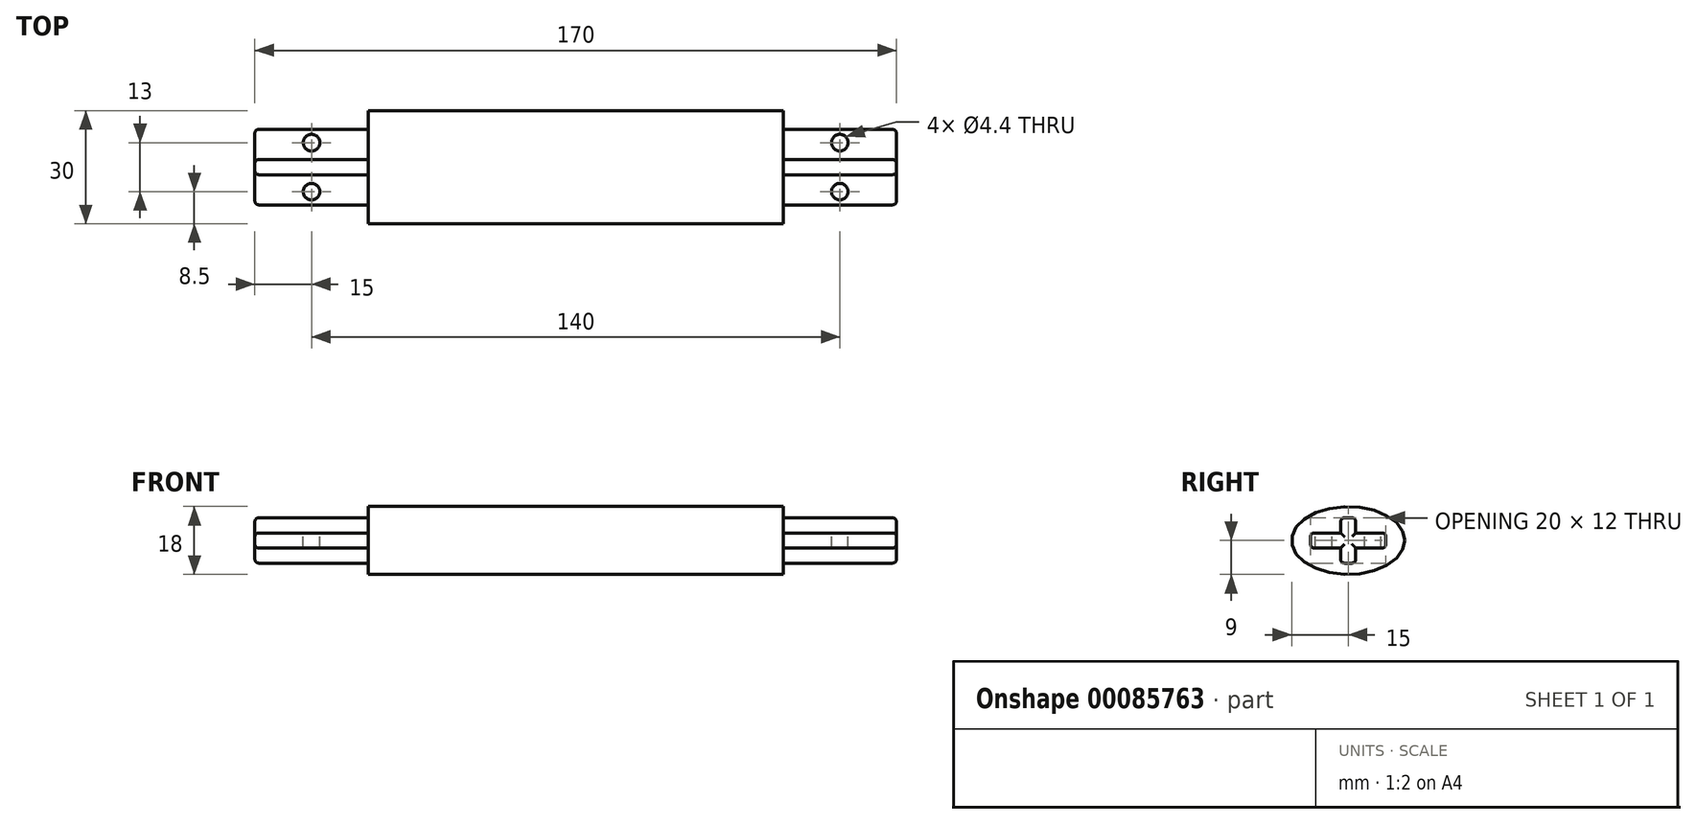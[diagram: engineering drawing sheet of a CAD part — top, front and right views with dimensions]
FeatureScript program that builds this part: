
annotation { "Feature Type Name" : "Feature", "Feature Type Description" : "" }
export const myFeature = defineFeature(function(context is Context, id is Id, definition is map)
    precondition{}
    {
        {
            var Q0;
            Q0=qCreatedBy(makeId("Right.planeOp"),FACE);
            var sketch = newSketch(context, id + "F0", { "sketchPlane" : qUnion([Q0])});
            skLineSegment(sketch, "E0", {"start": v(0, 6) * mm, "end": v(2, 6) * mm});
            skLineSegment(sketch, "E1", {"start": v(2, 6) * mm, "end": v(2, 2) * mm});
            skLineSegment(sketch, "E2", {"start": v(2, 2) * mm, "end": v(10, 2) * mm});
            skLineSegment(sketch, "E3", {"start": v(10, 2) * mm, "end": v(10, 0) * mm});
            skLineSegment(sketch, "E4.MirrorCS", {"start": v(-2, 2) * mm, "end": v(-10, 2) * mm});
            skLineSegment(sketch, "E5.MirrorCS", {"start": v(-2, 6) * mm, "end": v(-2, 2) * mm});
            skLineSegment(sketch, "E6.MirrorCS", {"start": v(0, 6) * mm, "end": v(-2, 6) * mm});
            skLineSegment(sketch, "E7.MirrorCS", {"start": v(-10, 2) * mm, "end": v(-10, 0) * mm});
            skLineSegment(sketch, "E8.MirrorCS", {"start": v(-2, -2) * mm, "end": v(-10, -2) * mm});
            skLineSegment(sketch, "E9.MirrorCS", {"start": v(-2, -6) * mm, "end": v(-2, -2) * mm});
            skLineSegment(sketch, "E10.MirrorCS", {"start": v(2, -6) * mm, "end": v(2, -2) * mm});
            skLineSegment(sketch, "E11.MirrorCS", {"start": v(0, -6) * mm, "end": v(-2, -6) * mm});
            skLineSegment(sketch, "E12.MirrorCS", {"start": v(10, -2) * mm, "end": v(10, 0) * mm});
            skLineSegment(sketch, "E13.MirrorCS", {"start": v(0, -6) * mm, "end": v(2, -6) * mm});
            skLineSegment(sketch, "E14.MirrorCS", {"start": v(-10, -2) * mm, "end": v(-10, 0) * mm});
            skLineSegment(sketch, "E15.MirrorCS", {"start": v(2, -2) * mm, "end": v(10, -2) * mm});
            skSolve(sketch);
        }
        {
            var Q0;
            Q0=makeQuery(id+"F0.imprint","IMPRINT",FACE,{"disambiguationData":[TD([[makeQuery(id+"F0.imprint","IMPRINT",EDGE,{"derivedFrom":sQuery(id+"F0.wireOp",EDGE,"E3")}),-1.0]])]});
            var Q1;
            Q1 = qConstructionFilter(qBodyType(qCreatedBy(id + "F0" ,EDGE), BodyType.WIRE), ConstructionObject.NO);
            extrude(context, id + "F1", {"entities" : qUnion([Q0]), "surfaceEntities" : qUnion([Q1]), "depth" : 170 * mm});
        }
        {
            var Q0;
            Q0=makeQuery(id+"F1.opExtrude","SWEPT_EDGE",EDGE,{"disambiguationData":[OSD([sQuery(id+"F0.wireOp",EDGE,"E1"),sQuery(id+"F0.wireOp",EDGE,"E0")])]});
            var Q1;
            Q1=makeQuery(id+"F1.opExtrude","SWEPT_EDGE",EDGE,{"disambiguationData":[OSD([sQuery(id+"F0.wireOp",EDGE,"E4.MirrorCS"),sQuery(id+"F0.wireOp",EDGE,"E7.MirrorCS")])]});
            var Q2;
            Q2=makeQuery(id+"F1.opExtrude","SWEPT_EDGE",EDGE,{"disambiguationData":[OSD([sQuery(id+"F0.wireOp",EDGE,"E6.MirrorCS"),sQuery(id+"F0.wireOp",EDGE,"E5.MirrorCS")])]});
            var Q3;
            Q3=makeQuery(id+"F1.opExtrude","SWEPT_EDGE",EDGE,{"disambiguationData":[OSD([sQuery(id+"F0.wireOp",EDGE,"E13.MirrorCS"),sQuery(id+"F0.wireOp",EDGE,"E10.MirrorCS")])]});
            var Q4;
            Q4=makeQuery(id+"F1.opExtrude","SWEPT_EDGE",EDGE,{"disambiguationData":[OSD([sQuery(id+"F0.wireOp",EDGE,"E12.MirrorCS"),sQuery(id+"F0.wireOp",EDGE,"E15.MirrorCS")])]});
            var Q5;
            Q5=makeQuery(id+"F1.opExtrude","SWEPT_EDGE",EDGE,{"disambiguationData":[OSD([sQuery(id+"F0.wireOp",EDGE,"E3"),sQuery(id+"F0.wireOp",EDGE,"E2")])]});
            var Q6;
            Q6=makeQuery(id+"F1.opExtrude","SWEPT_EDGE",EDGE,{"disambiguationData":[OSD([sQuery(id+"F0.wireOp",EDGE,"E14.MirrorCS"),sQuery(id+"F0.wireOp",EDGE,"E8.MirrorCS")])]});
            var Q7;
            Q7=makeQuery(id+"F1.opExtrude","SWEPT_EDGE",EDGE,{"disambiguationData":[OSD([sQuery(id+"F0.wireOp",EDGE,"E9.MirrorCS"),sQuery(id+"F0.wireOp",EDGE,"E11.MirrorCS")])]});
            var Q8;
            Q8=makeQuery(id+"F1.opExtrude","CAP_EDGE",EDGE,{"disambiguationData":[OSD([sQuery(id+"F0.wireOp",EDGE,"E5.MirrorCS")])],"isStart":false});
            var Q9;
            Q9=makeQuery(id+"F1.opExtrude","CAP_EDGE",EDGE,{"disambiguationData":[OSD([sQuery(id+"F0.wireOp",EDGE,"E1")])],"isStart":false});
            var Q10;
            Q10=makeQuery(id+"F1.opExtrude","CAP_EDGE",EDGE,{"disambiguationData":[OSD([sQuery(id+"F0.wireOp",EDGE,"E2")])],"isStart":false});
            var Q11;
            Q11=makeQuery(id+"F1.opExtrude","CAP_FACE",FACE,{"disambiguationData":[OSD([sQuery(id+"F0.wireOp",EDGE,"E3"),sQuery(id+"F0.wireOp",EDGE,"E4.MirrorCS"),sQuery(id+"F0.wireOp",EDGE,"E7.MirrorCS"),sQuery(id+"F0.wireOp",EDGE,"E2"),sQuery(id+"F0.wireOp",EDGE,"E6.MirrorCS"),sQuery(id+"F0.wireOp",EDGE,"E1"),sQuery(id+"F0.wireOp",EDGE,"E5.MirrorCS"),sQuery(id+"F0.wireOp",EDGE,"E0"),sQuery(id+"F0.wireOp",EDGE,"E13.MirrorCS"),sQuery(id+"F0.wireOp",EDGE,"E9.MirrorCS"),sQuery(id+"F0.wireOp",EDGE,"E12.MirrorCS"),sQuery(id+"F0.wireOp",EDGE,"E14.MirrorCS"),sQuery(id+"F0.wireOp",EDGE,"E10.MirrorCS"),sQuery(id+"F0.wireOp",EDGE,"E15.MirrorCS"),sQuery(id+"F0.wireOp",EDGE,"E11.MirrorCS"),sQuery(id+"F0.wireOp",EDGE,"E8.MirrorCS")])],"isStart":false});
            var Q12;
            Q12=makeQuery(id+"F1.opExtrude","CAP_EDGE",EDGE,{"disambiguationData":[OSD([sQuery(id+"F0.wireOp",EDGE,"E4.MirrorCS")])],"isStart":false});
            var Q13;
            Q13=makeQuery(id+"F1.opExtrude","CAP_EDGE",EDGE,{"disambiguationData":[OSD([sQuery(id+"F0.wireOp",EDGE,"E5.MirrorCS")])],"isStart":true});
            var Q14;
            Q14=makeQuery(id+"F1.opExtrude","CAP_EDGE",EDGE,{"disambiguationData":[OSD([sQuery(id+"F0.wireOp",EDGE,"E6.MirrorCS"),sQuery(id+"F0.wireOp",EDGE,"E0")])],"isStart":true});
            var Q15;
            Q15=makeQuery(id+"F1.opExtrude","CAP_EDGE",EDGE,{"disambiguationData":[OSD([sQuery(id+"F0.wireOp",EDGE,"E1")])],"isStart":true});
            var Q16;
            Q16=makeQuery(id+"F1.opExtrude","CAP_EDGE",EDGE,{"disambiguationData":[OSD([sQuery(id+"F0.wireOp",EDGE,"E4.MirrorCS")])],"isStart":true});
            var Q17;
            Q17=makeQuery(id+"F1.opExtrude","CAP_EDGE",EDGE,{"disambiguationData":[OSD([sQuery(id+"F0.wireOp",EDGE,"E8.MirrorCS")])],"isStart":true});
            var Q18;
            Q18=makeQuery(id+"F1.opExtrude","CAP_EDGE",EDGE,{"disambiguationData":[OSD([sQuery(id+"F0.wireOp",EDGE,"E7.MirrorCS"),sQuery(id+"F0.wireOp",EDGE,"E14.MirrorCS")])],"isStart":true});
            var Q19;
            Q19=makeQuery(id+"F1.opExtrude","CAP_EDGE",EDGE,{"disambiguationData":[OSD([sQuery(id+"F0.wireOp",EDGE,"E9.MirrorCS")])],"isStart":true});
            var Q20;
            Q20=makeQuery(id+"F1.opExtrude","CAP_EDGE",EDGE,{"disambiguationData":[OSD([sQuery(id+"F0.wireOp",EDGE,"E10.MirrorCS")])],"isStart":true});
            var Q21;
            Q21=makeQuery(id+"F1.opExtrude","CAP_EDGE",EDGE,{"disambiguationData":[OSD([sQuery(id+"F0.wireOp",EDGE,"E15.MirrorCS")])],"isStart":true});
            var Q22;
            Q22=makeQuery(id+"F1.opExtrude","CAP_EDGE",EDGE,{"disambiguationData":[OSD([sQuery(id+"F0.wireOp",EDGE,"E3"),sQuery(id+"F0.wireOp",EDGE,"E12.MirrorCS")])],"isStart":true});
            var Q23;
            Q23=makeQuery(id+"F1.opExtrude","CAP_EDGE",EDGE,{"disambiguationData":[OSD([sQuery(id+"F0.wireOp",EDGE,"E2")])],"isStart":true});
            var Q24;
            Q24=makeQuery(id+"F1.opExtrude","CAP_EDGE",EDGE,{"disambiguationData":[OSD([sQuery(id+"F0.wireOp",EDGE,"E13.MirrorCS"),sQuery(id+"F0.wireOp",EDGE,"E11.MirrorCS")])],"isStart":true});
            fillet(context, id + "F2", {"entities" : qUnion([Q0, Q1, Q2, Q3, Q4, Q5, Q6, Q7, Q8, Q9, Q10, Q11, Q12, Q13, Q14, Q15, Q16, Q17, Q18, Q19, Q20, Q21, Q22, Q23, Q24]), "radius" : 1 * mm, "tangentPropagation" : true, "allowEdgeOverflow" : false});
        }
        {
            var Q0;
            Q0=qCreatedBy(makeId("Top.planeOp"),FACE);
            cPlane(context, id + "F3", {"entities" : qUnion([Q0]), "cplaneType" : CPlaneType.OFFSET, "offset" : 15 * mm, "width" : 150 * mm, "height" : 150 * mm});
        }
        {
            var Q0;
            Q0=qCreatedBy(id+"F3.planeOp",FACE);
            var sketch = newSketch(context, id + "F4", { "sketchPlane" : qUnion([Q0])});
            skPoint(sketch, "E16", {"position": v(15, 6.5) * mm});
            skPoint(sketch, "E17", {"position": v(15, -6.5) * mm});
            skPoint(sketch, "E18", {"position": v(155, 6.5) * mm});
            skPoint(sketch, "E19", {"position": v(155, -6.5) * mm});
            skSolve(sketch);
        }
        {
            var Q0;
            Q0=qCreatedBy(makeId("Right.planeOp"),FACE);
            cPlane(context, id + "F5", {"entities" : qUnion([Q0]), "cplaneType" : CPlaneType.OFFSET, "offset" : 30 * mm, "width" : 150 * mm, "height" : 150 * mm});
        }
        {
            var Q0;
            Q0=qCreatedBy(id+"F5.planeOp",FACE);
            var sketch = newSketch(context, id + "F6", { "sketchPlane" : qUnion([Q0])});
            skEllipse(sketch, "E20", {"center": v(0, 0) * mm, "majorRadius": 15 * mm, "minorRadius": 9 * mm, "majorAxis": v(1, 0)});
            skLineSegment(sketch, "E21", {"start": v(0, 0) * mm, "end": v(15, 0) * mm});
            skLineSegment(sketch, "E22", {"start": v(0, 0) * mm, "end": v(0, 9) * mm});
            skSolve(sketch);
        }
        {
            var Q0;
            {var subQ0=sQuery(id+"F6.wireOp",EDGE,"E21");Q0=makeQuery(id+"F6.imprint","IMPRINT",FACE,{"disambiguationData":[TD([[makeQuery(id+"F6.imprint","IMPRINT",EDGE,{"derivedFrom":subQ0}),-1.0]])]});}
            var Q1;
            {var subQ0=sQuery(id+"F6.wireOp",EDGE,"E21");Q1=makeQuery(id+"F6.imprint","IMPRINT",FACE,{"disambiguationData":[TD([[makeQuery(id+"F6.imprint","IMPRINT",EDGE,{"derivedFrom":subQ0}),1.0]])]});}
            extrude(context, id + "F7", {"entities" : qUnion([Q0, Q1]), "operationType" : NewBodyOperationType.ADD, "depth" : 110 * mm});
        }
        {
            var Q0;
            Q0=sQuery(id+"F4.wireOp",VERTEX,"E16");
            var Q1;
            Q1=sQuery(id+"F4.wireOp",VERTEX,"E17");
            var Q2;
            Q2=sQuery(id+"F4.wireOp",VERTEX,"E19");
            var Q3;
            Q3=sQuery(id+"F4.wireOp",VERTEX,"E18");
            var Q4;
            Q4=makeQuery(id+"F1.opExtrude","SWEPT_BODY",BODY,{"disambiguationData":[OSD([sQuery(id+"F0.wireOp",EDGE,"E3"),sQuery(id+"F0.wireOp",EDGE,"E4.MirrorCS"),sQuery(id+"F0.wireOp",EDGE,"E7.MirrorCS"),sQuery(id+"F0.wireOp",EDGE,"E2"),sQuery(id+"F0.wireOp",EDGE,"E6.MirrorCS"),sQuery(id+"F0.wireOp",EDGE,"E1"),sQuery(id+"F0.wireOp",EDGE,"E5.MirrorCS"),sQuery(id+"F0.wireOp",EDGE,"E0"),sQuery(id+"F0.wireOp",EDGE,"E13.MirrorCS"),sQuery(id+"F0.wireOp",EDGE,"E9.MirrorCS"),sQuery(id+"F0.wireOp",EDGE,"E12.MirrorCS"),sQuery(id+"F0.wireOp",EDGE,"E14.MirrorCS"),sQuery(id+"F0.wireOp",EDGE,"E10.MirrorCS"),sQuery(id+"F0.wireOp",EDGE,"E15.MirrorCS"),sQuery(id+"F0.wireOp",EDGE,"E11.MirrorCS"),sQuery(id+"F0.wireOp",EDGE,"E8.MirrorCS")])]});
            hole(context, id + "F8", {"style" : HoleStyle.C_BORE, "endStyle" : HoleEndStyle.BLIND, "holeDiameter" : 4.4 * mm, "cBoreDiameter" : 4.4 * mm, "cBoreDepth" : 4 * mm, "holeDepth" : 30 * mm, "locations" : qUnion([Q0, Q1, Q2, Q3]), "scope" : qUnion([Q4])});
        }
    });
